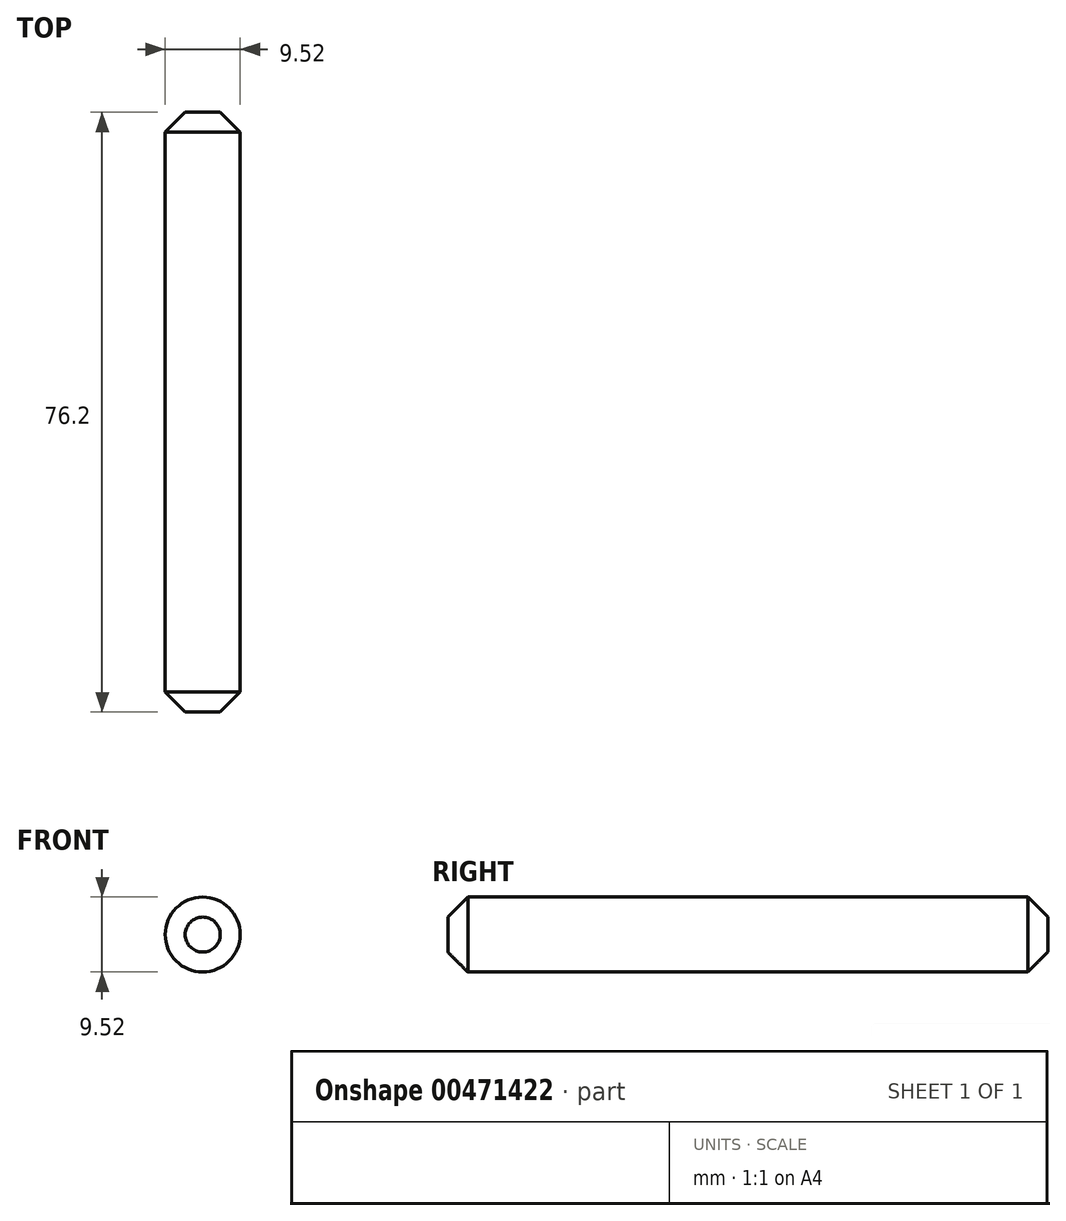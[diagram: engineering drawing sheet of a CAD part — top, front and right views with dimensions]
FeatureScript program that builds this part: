
annotation { "Feature Type Name" : "Feature", "Feature Type Description" : "" }
export const myFeature = defineFeature(function(context is Context, id is Id, definition is map)
    precondition{}
    {
        {
            var Q0;
            Q0=qCreatedBy(makeId("Front.planeOp"),FACE);
            var sketch = newSketch(context, id + "F0", { "sketchPlane" : qUnion([Q0])});
            skCircle(sketch, "E0", {"center": v(0, 0) * mm, "radius": 4.76 * mm});
            skSolve(sketch);
        }
        {
            var Q0;
            Q0 = qSketchRegion(id + "F0", true);
            extrude(context, id + "F1", {"entities" : qUnion([Q0]), "endBound" : BoundingType.SYMMETRIC, "depth" : 76.2 * mm});
        }
        {
            var Q0;
            Q0=makeQuery(id+"F1.opExtrude","CAP_EDGE",EDGE,{"disambiguationData":[OSD([sQuery(id+"F0.wireOp",EDGE,"E0")])],"isStart":false});
            var Q1;
            Q1=makeQuery(id+"F1.opExtrude","CAP_EDGE",EDGE,{"disambiguationData":[OSD([sQuery(id+"F0.wireOp",EDGE,"E0")])],"isStart":true});
            chamfer(context, id + "F2", {"entities" : qUnion([Q0, Q1]), "width" : 2.54 * mm, "tangentPropagation" : true});
        }
    });
